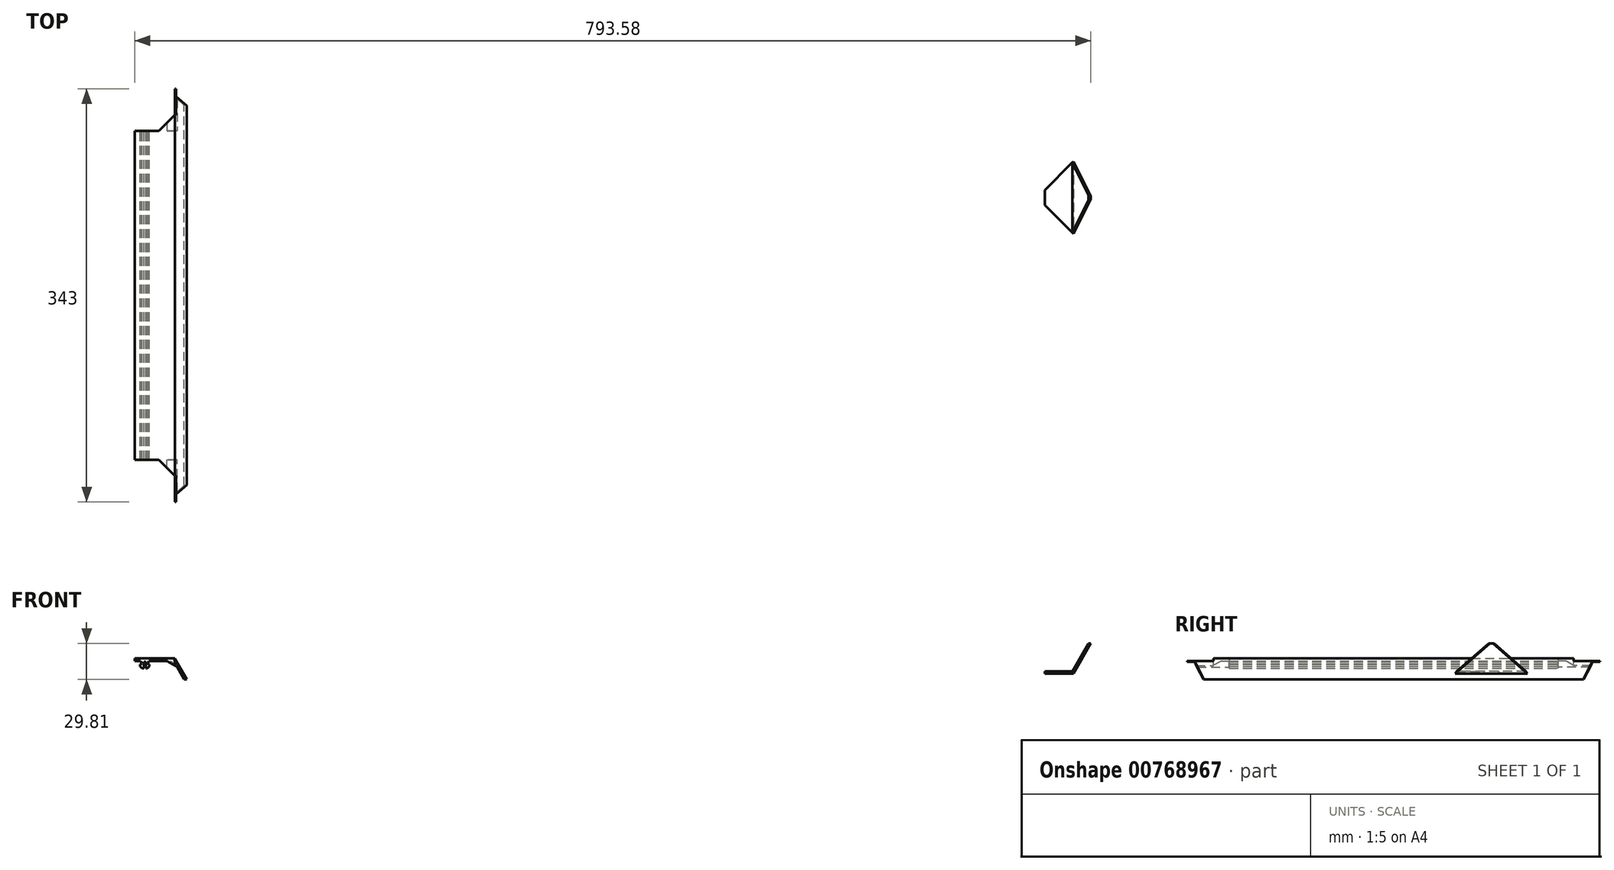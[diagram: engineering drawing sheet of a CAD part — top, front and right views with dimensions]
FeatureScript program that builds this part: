
annotation { "Feature Type Name" : "Feature", "Feature Type Description" : "" }
export const myFeature = defineFeature(function(context is Context, id is Id, definition is map)
    precondition{}
    {
        {
            var Q0;
            Q0=qCreatedBy(makeId("Front.planeOp"),FACE);
            var sketch = newSketch(context, id + "F0", { "sketchPlane" : qUnion([Q0])});
            skLineSegment(sketch, "E0", {"start": v(-133.25, 6.08) * mm, "end": v(-131.79, 4.46) * mm});
            skLineSegment(sketch, "E1", {"start": v(-131.79, 4.46) * mm, "end": v(-130.32, 4.46) * mm});
            skLineSegment(sketch, "E2", {"start": v(-132.9, 10.57) * mm, "end": v(-131.79, 8.3) * mm});
            skLineSegment(sketch, "E3", {"start": v(-133.25, 7.64) * mm, "end": v(-131.79, 8.3) * mm});
            skLineSegment(sketch, "E4", {"start": v(-130.32, 4.46) * mm, "end": v(-130.32, 9.87) * mm});
            skLineSegment(sketch, "E5", {"start": v(-130.32, 9.87) * mm, "end": v(-127.68, 9.87) * mm});
            skLineSegment(sketch, "E6", {"start": v(-134.43, 10.57) * mm, "end": v(-132.9, 10.57) * mm});
            skLineSegment(sketch, "E7.MirrorCS", {"start": v(-124.57, 10.57) * mm, "end": v(-126.1, 10.57) * mm});
            skLineSegment(sketch, "E8.MirrorCS", {"start": v(-126.1, 10.57) * mm, "end": v(-127.2, 8.3) * mm});
            skLineSegment(sketch, "E9.MirrorCS", {"start": v(-125.74, 7.63) * mm, "end": v(-127.2, 8.3) * mm});
            skLineSegment(sketch, "E10.MirrorCS", {"start": v(-125.74, 6.1) * mm, "end": v(-127.2, 4.46) * mm});
            skLineSegment(sketch, "E11.MirrorCS", {"start": v(-127.2, 4.46) * mm, "end": v(-128.68, 4.46) * mm});
            skLineSegment(sketch, "E12.MirrorCS", {"start": v(-128.68, 4.46) * mm, "end": v(-128.68, 9.87) * mm});
            skLineSegment(sketch, "E13.MirrorCS", {"start": v(-128.68, 9.87) * mm, "end": v(-129.5, 9.87) * mm});
            skLineSegment(sketch, "E14", {"start": v(-134.43, 12.57) * mm, "end": v(-124.57, 12.57) * mm});
            skLineSegment(sketch, "E15", {"start": v(-127.68, 9.87) * mm, "end": v(-117.68, 9.87) * mm, "construction": true});
            skLineSegment(sketch, "E16.bottom", {"start": v(-124.57, 12.57) * mm, "end": v(-104.57, 12.57) * mm});
            skLineSegment(sketch, "E16.top", {"start": v(-119.57, 10.57) * mm, "end": v(-111.25, 10.57) * mm});
            skLineSegment(sketch, "E17", {"start": v(-104.57, 12.57) * mm, "end": v(-94.7, -4.81) * mm});
            skLineSegment(sketch, "E18", {"start": v(-94.7, -4.81) * mm, "end": v(-96.7, -4.81) * mm});
            skLineSegment(sketch, "E19", {"start": v(-96.7, -4.81) * mm, "end": v(-102.56, 5.51) * mm});
            skLineSegment(sketch, "E20", {"start": v(-124.57, 10.57) * mm, "end": v(-119.57, 10.57) * mm});
            skLineSegment(sketch, "E21", {"start": v(-127.68, 9.87) * mm, "end": v(-137.68, 9.87) * mm, "construction": true});
            skLineSegment(sketch, "E22.bottom", {"start": v(-134.43, 12.57) * mm, "end": v(-137.68, 12.57) * mm});
            skLineSegment(sketch, "E22.top", {"start": v(-134.43, 10.57) * mm, "end": v(-137.68, 10.57) * mm});
            skLineSegment(sketch, "E22.right", {"start": v(-137.68, 12.57) * mm, "end": v(-137.68, 10.57) * mm});
            skLineSegment(sketch, "E23", {"start": v(-133.25, 7.64) * mm, "end": v(-133.25, 6.08) * mm});
            skLineSegment(sketch, "E24", {"start": v(-125.74, 7.63) * mm, "end": v(-125.74, 6.1) * mm});
            skPoint(sketch, "E25.visualSharp", {"position": v(-105.43, 10.57) * mm});
            skArc(sketch, "E25.filletArc", {"start": v(-102.56, 5.51) * mm, "mid": v(-106.22, 9.22) * mm, "end": v(-111.25, 10.57) * mm});
            skSolve(sketch);
        }
        {
            var Q0;
            Q0 = qSketchRegion(id + "F0", true);
            extrude(context, id + "F1", {"entities" : qUnion([Q0]), "depth" : 273 * mm, "offsetDistance" : 25 * mm});
        }
        {
            var Q0;
            Q0=qCreatedBy(makeId("Top.planeOp"),FACE);
            var sketch = newSketch(context, id + "F2", { "sketchPlane" : qUnion([Q0])});
            skLineSegment(sketch, "E26.bottom", {"start": v(617.8, -25.34) * mm, "end": v(677.8, -25.34) * mm});
            skLineSegment(sketch, "E26.top", {"start": v(617.8, -85.34) * mm, "end": v(677.8, -85.34) * mm});
            skLineSegment(sketch, "E26.left", {"start": v(617.8, -25.34) * mm, "end": v(617.8, -85.34) * mm});
            skLineSegment(sketch, "E26.right", {"start": v(677.8, -25.34) * mm, "end": v(677.8, -85.34) * mm});
            skSolve(sketch);
        }
        {
            var Q0;
            Q0 = qSketchRegion(id + "F2", true);
            extrude(context, id + "F3", {"entities" : qUnion([Q0]), "depth" : 25 * mm, "offsetDistance" : 25 * mm});
        }
        {
            var Q0;
            Q0=makeQuery(id+"F3.opExtrude","SWEPT_FACE",FACE,{"disambiguationData":[OSD([sQuery(id+"F2.wireOp",EDGE,"E26.top")])]});
            var sketch = newSketch(context, id + "F4", { "sketchPlane" : qUnion([Q0])});
            skLineSegment(sketch, "E27", {"start": v(641.7, 0) * mm, "end": v(655.9, 25) * mm});
            skLineSegment(sketch, "E28", {"start": v(653.9, 25) * mm, "end": v(640.84, 2) * mm});
            skLineSegment(sketch, "E29", {"start": v(617.8, 2) * mm, "end": v(640.84, 2) * mm});
            skPoint(sketch, "E30.orphan", {"position": v(639.7, 0) * mm});
            skLineSegment(sketch, "E31", {"start": v(617.8, 2) * mm, "end": v(617.8, 25) * mm});
            skLineSegment(sketch, "E32", {"start": v(617.8, 25) * mm, "end": v(653.9, 25) * mm});
            skLineSegment(sketch, "E33", {"start": v(655.9, 25) * mm, "end": v(677.8, 25) * mm});
            skLineSegment(sketch, "E34", {"start": v(677.8, 25) * mm, "end": v(677.8, 0) * mm});
            skLineSegment(sketch, "E35", {"start": v(677.8, 0) * mm, "end": v(641.7, 0) * mm});
            skSolve(sketch);
        }
        {
            var Q0;
            Q0 = qSketchRegion(id + "F4", true);
            extrude(context, id + "F5", {"entities" : qUnion([Q0]), "operationType" : NewBodyOperationType.REMOVE, "oppositeDirection" : true, "depth" : 60 * mm, "offsetDistance" : 25 * mm});
        }
        {
            var Q0;
            Q0=makeQuery(id+"F3.opExtrude","CAP_FACE",FACE,{"disambiguationData":[OSD([sQuery(id+"F2.wireOp",EDGE,"E26.bottom"),sQuery(id+"F2.wireOp",EDGE,"E26.top"),sQuery(id+"F2.wireOp",EDGE,"E26.left"),sQuery(id+"F2.wireOp",EDGE,"E26.right")])],"isStart":true});
            var sketch = newSketch(context, id + "F6", { "sketchPlane" : qUnion([Q0])});
            skLineSegment(sketch, "E36", {"start": v(641.7, 85.34) * mm, "end": v(617.8, 61.44) * mm});
            skLineSegment(sketch, "E37", {"start": v(641.7, 85.34) * mm, "end": v(617.8, 85.34) * mm});
            skLineSegment(sketch, "E38", {"start": v(641.7, 25.34) * mm, "end": v(617.8, 49.24) * mm});
            skLineSegment(sketch, "E39", {"start": v(641.7, 25.34) * mm, "end": v(617.8, 25.34) * mm});
            skLineSegment(sketch, "E40", {"start": v(617.8, 25.34) * mm, "end": v(617.8, 49.24) * mm});
            skLineSegment(sketch, "E41", {"start": v(617.8, 85.34) * mm, "end": v(617.8, 61.44) * mm});
            skSolve(sketch);
        }
        {
            var Q0;
            Q0 = qSketchRegion(id + "F6", true);
            extrude(context, id + "F7", {"entities" : qUnion([Q0]), "operationType" : NewBodyOperationType.REMOVE, "oppositeDirection" : true, "depth" : 25 * mm, "offsetDistance" : 25 * mm});
        }
        {
            var Q0;
            Q0=makeQuery(id+"F5.boolean.opBoolean","COPY",FACE,{"derivedFrom":makeQuery(id+"F5.opExtrude","SWEPT_FACE",FACE,{"disambiguationData":[OSD([sQuery(id+"F4.wireOp",EDGE,"E27")])]})});
            var sketch = newSketch(context, id + "F8", { "sketchPlane" : qUnion([Q0])});
            skLineSegment(sketch, "E42", {"start": v(-25.34, 317.01) * mm, "end": v(-25.34, 345.76) * mm});
            skLineSegment(sketch, "E43", {"start": v(-25.34, 317.01) * mm, "end": v(-54.09, 345.76) * mm});
            skLineSegment(sketch, "E44", {"start": v(-85.34, 345.76) * mm, "end": v(-85.34, 317.01) * mm});
            skLineSegment(sketch, "E45", {"start": v(-85.34, 317.01) * mm, "end": v(-56.58, 345.76) * mm});
            skLineSegment(sketch, "E46", {"start": v(-25.34, 345.76) * mm, "end": v(-54.09, 345.76) * mm});
            skLineSegment(sketch, "E47", {"start": v(-56.58, 345.76) * mm, "end": v(-85.34, 345.76) * mm});
            skSolve(sketch);
        }
        {
            var Q0;
            Q0 = qSketchRegion(id + "F8", true);
            extrude(context, id + "F9", {"entities" : qUnion([Q0]), "operationType" : NewBodyOperationType.REMOVE, "oppositeDirection" : true, "depth" : 25 * mm, "offsetDistance" : 25 * mm});
        }
        {
            var Q0;
            Q0=makeQuery(id+"F1.opExtrude","CAP_FACE",FACE,{"disambiguationData":[OSD([sQuery(id+"F0.wireOp",EDGE,"E0"),sQuery(id+"F0.wireOp",EDGE,"E1"),sQuery(id+"F0.wireOp",EDGE,"E2"),sQuery(id+"F0.wireOp",EDGE,"E3"),sQuery(id+"F0.wireOp",EDGE,"E4"),sQuery(id+"F0.wireOp",EDGE,"E5"),sQuery(id+"F0.wireOp",EDGE,"E6"),sQuery(id+"F0.wireOp",EDGE,"E7.MirrorCS"),sQuery(id+"F0.wireOp",EDGE,"E8.MirrorCS"),sQuery(id+"F0.wireOp",EDGE,"E9.MirrorCS"),sQuery(id+"F0.wireOp",EDGE,"E10.MirrorCS"),sQuery(id+"F0.wireOp",EDGE,"E11.MirrorCS"),sQuery(id+"F0.wireOp",EDGE,"E12.MirrorCS"),sQuery(id+"F0.wireOp",EDGE,"E13.MirrorCS"),sQuery(id+"F0.wireOp",EDGE,"E14"),sQuery(id+"F0.wireOp",EDGE,"E16.bottom"),sQuery(id+"F0.wireOp",EDGE,"E16.top"),sQuery(id+"F0.wireOp",EDGE,"E17"),sQuery(id+"F0.wireOp",EDGE,"E18"),sQuery(id+"F0.wireOp",EDGE,"E19"),sQuery(id+"F0.wireOp",EDGE,"E20"),sQuery(id+"F0.wireOp",EDGE,"E22.bottom"),sQuery(id+"F0.wireOp",EDGE,"E22.top"),sQuery(id+"F0.wireOp",EDGE,"E22.right"),sQuery(id+"F0.wireOp",EDGE,"E23"),sQuery(id+"F0.wireOp",EDGE,"E24"),sQuery(id+"F0.wireOp",EDGE,"E25.filletArc")])],"isStart":true});
            var sketch = newSketch(context, id + "F10", { "sketchPlane" : qUnion([Q0])});
            skLineSegment(sketch, "E48", {"start": v(96.7, -4.81) * mm, "end": v(94.7, -4.81) * mm});
            skLineSegment(sketch, "E49", {"start": v(94.7, -4.81) * mm, "end": v(104.57, 12.57) * mm});
            skLineSegment(sketch, "E50", {"start": v(104.57, 12.57) * mm, "end": v(117.68, 12.57) * mm});
            skLineSegment(sketch, "E51", {"start": v(117.68, 10.57) * mm, "end": v(111.25, 10.57) * mm});
            skLineSegment(sketch, "E52", {"start": v(111.25, 10.57) * mm, "end": v(102.56, 5.51) * mm});
            skLineSegment(sketch, "E53", {"start": v(102.56, 5.51) * mm, "end": v(96.7, -4.81) * mm});
            skLineSegment(sketch, "E54", {"start": v(137.68, 11.57) * mm, "end": v(117.68, 11.57) * mm, "construction": true});
            skLineSegment(sketch, "E55", {"start": v(117.68, 12.57) * mm, "end": v(117.68, 10.57) * mm});
            skPoint(sketch, "E56.end.orphan", {"position": v(119.44, 10.57) * mm});
            skSolve(sketch);
        }
        {
            var Q0;
            Q0 = qSketchRegion(id + "F10", true);
            extrude(context, id + "F11", {"entities" : qUnion([Q0]), "operationType" : NewBodyOperationType.ADD, "depth" : 35 * mm, "offsetDistance" : 25 * mm});
        }
        {
            var Q0;
            Q0=makeQuery(id+"F1.opExtrude","CAP_FACE",FACE,{"disambiguationData":[OSD([sQuery(id+"F0.wireOp",EDGE,"E0"),sQuery(id+"F0.wireOp",EDGE,"E1"),sQuery(id+"F0.wireOp",EDGE,"E2"),sQuery(id+"F0.wireOp",EDGE,"E3"),sQuery(id+"F0.wireOp",EDGE,"E4"),sQuery(id+"F0.wireOp",EDGE,"E5"),sQuery(id+"F0.wireOp",EDGE,"E6"),sQuery(id+"F0.wireOp",EDGE,"E7.MirrorCS"),sQuery(id+"F0.wireOp",EDGE,"E8.MirrorCS"),sQuery(id+"F0.wireOp",EDGE,"E9.MirrorCS"),sQuery(id+"F0.wireOp",EDGE,"E10.MirrorCS"),sQuery(id+"F0.wireOp",EDGE,"E11.MirrorCS"),sQuery(id+"F0.wireOp",EDGE,"E12.MirrorCS"),sQuery(id+"F0.wireOp",EDGE,"E13.MirrorCS"),sQuery(id+"F0.wireOp",EDGE,"E14"),sQuery(id+"F0.wireOp",EDGE,"E16.bottom"),sQuery(id+"F0.wireOp",EDGE,"E16.top"),sQuery(id+"F0.wireOp",EDGE,"E17"),sQuery(id+"F0.wireOp",EDGE,"E18"),sQuery(id+"F0.wireOp",EDGE,"E19"),sQuery(id+"F0.wireOp",EDGE,"E20"),sQuery(id+"F0.wireOp",EDGE,"E22.bottom"),sQuery(id+"F0.wireOp",EDGE,"E22.top"),sQuery(id+"F0.wireOp",EDGE,"E22.right"),sQuery(id+"F0.wireOp",EDGE,"E23"),sQuery(id+"F0.wireOp",EDGE,"E24"),sQuery(id+"F0.wireOp",EDGE,"E25.filletArc")])],"isStart":false});
            var sketch = newSketch(context, id + "F12", { "sketchPlane" : qUnion([Q0])});
            skLineSegment(sketch, "E57", {"start": v(-137.68, 11.57) * mm, "end": v(-117.68, 11.57) * mm, "construction": true});
            skLineSegment(sketch, "E58", {"start": v(-117.68, 12.57) * mm, "end": v(-117.68, 10.57) * mm});
            skLineSegment(sketch, "E59", {"start": v(-117.68, 10.57) * mm, "end": v(-111.25, 10.57) * mm});
            skLineSegment(sketch, "E60", {"start": v(-111.25, 10.57) * mm, "end": v(-102.56, 5.51) * mm});
            skLineSegment(sketch, "E61", {"start": v(-102.56, 5.51) * mm, "end": v(-96.7, -4.81) * mm});
            skLineSegment(sketch, "E62", {"start": v(-96.7, -4.81) * mm, "end": v(-94.7, -4.81) * mm});
            skLineSegment(sketch, "E63", {"start": v(-94.7, -4.81) * mm, "end": v(-104.57, 12.57) * mm});
            skLineSegment(sketch, "E64", {"start": v(-104.57, 12.57) * mm, "end": v(-117.68, 12.57) * mm});
            skSolve(sketch);
        }
        {
            var Q0;
            Q0 = qSketchRegion(id + "F12", true);
            extrude(context, id + "F13", {"entities" : qUnion([Q0]), "operationType" : NewBodyOperationType.ADD, "depth" : 35 * mm, "offsetDistance" : 25 * mm});
        }
        {
            var Q0;
            Q0=makeQuery(id+"F13.boolean.opBoolean","MERGE",FACE,{"derivedFrom":[makeQuery(id+"F11.boolean.opBoolean","MERGE",FACE,{"derivedFrom":[makeQuery(id+"F1.opExtrude","SWEPT_FACE",FACE,{"disambiguationData":[OSD([sQuery(id+"F0.wireOp",EDGE,"E14"),sQuery(id+"F0.wireOp",EDGE,"E16.bottom"),sQuery(id+"F0.wireOp",EDGE,"E22.bottom")])]}),makeQuery(id+"F11.opExtrude","SWEPT_FACE",FACE,{"disambiguationData":[OSD([sQuery(id+"F10.wireOp",EDGE,"E50")])]})]}),makeQuery(id+"F13.opExtrude","SWEPT_FACE",FACE,{"disambiguationData":[OSD([sQuery(id+"F12.wireOp",EDGE,"E64")])]})]});
            var sketch = newSketch(context, id + "F14", { "sketchPlane" : qUnion([Q0])});
            skLineSegment(sketch, "E65", {"start": v(-117.68, 0) * mm, "end": v(-109.5, 0) * mm});
            skLineSegment(sketch, "E66", {"start": v(-117.68, 0) * mm, "end": v(-104.57, 13.1) * mm});
            skLineSegment(sketch, "E67", {"start": v(-104.57, 13.1) * mm, "end": v(-104.57, 35) * mm});
            skLineSegment(sketch, "E68", {"start": v(-104.57, 35) * mm, "end": v(-117.68, 35) * mm});
            skLineSegment(sketch, "E69", {"start": v(-117.68, 35) * mm, "end": v(-117.68, 0) * mm});
            skLineSegment(sketch, "E70", {"start": v(-117.68, -273) * mm, "end": v(-110.08, -273) * mm});
            skLineSegment(sketch, "E71", {"start": v(-117.68, -273) * mm, "end": v(-104.57, -286.1) * mm});
            skLineSegment(sketch, "E72", {"start": v(-104.57, -286.1) * mm, "end": v(-104.57, -308) * mm});
            skLineSegment(sketch, "E73", {"start": v(-104.57, -308) * mm, "end": v(-117.68, -308) * mm});
            skLineSegment(sketch, "E74", {"start": v(-117.68, -308) * mm, "end": v(-117.68, -273) * mm});
            skSolve(sketch);
        }
        {
            var Q0;
            Q0 = qSketchRegion(id + "F14", true);
            extrude(context, id + "F15", {"entities" : qUnion([Q0]), "operationType" : NewBodyOperationType.REMOVE, "oppositeDirection" : true, "depth" : 25 * mm, "offsetDistance" : 25 * mm});
        }
        {
            var Q0;
            Q0=makeQuery(id+"F13.opExtrude","CAP_FACE",FACE,{"disambiguationData":[OSD([sQuery(id+"F12.wireOp",EDGE,"E58"),sQuery(id+"F12.wireOp",EDGE,"E59"),sQuery(id+"F12.wireOp",EDGE,"E60"),sQuery(id+"F12.wireOp",EDGE,"E61"),sQuery(id+"F12.wireOp",EDGE,"E62"),sQuery(id+"F12.wireOp",EDGE,"E63"),sQuery(id+"F12.wireOp",EDGE,"E64")])],"isStart":false});
            var sketch = newSketch(context, id + "F16", { "sketchPlane" : qUnion([Q0])});
            skLineSegment(sketch, "E75.bottom", {"start": v(-83.95, 21.16) * mm, "end": v(-118.74, 21.16) * mm});
            skLineSegment(sketch, "E75.top", {"start": v(-83.95, 10.51) * mm, "end": v(-118.74, 10.51) * mm});
            skLineSegment(sketch, "E75.left", {"start": v(-83.95, 21.16) * mm, "end": v(-83.95, 10.51) * mm});
            skLineSegment(sketch, "E75.right", {"start": v(-118.74, 21.16) * mm, "end": v(-118.74, 10.51) * mm});
            skSolve(sketch);
        }
        {
            var Q0;
            Q0 = qSketchRegion(id + "F16", true);
            extrude(context, id + "F17", {"entities" : qUnion([Q0]), "operationType" : NewBodyOperationType.REMOVE, "oppositeDirection" : true, "depth" : 22 * mm, "offsetDistance" : 25 * mm});
        }
        {
            var Q0;
            Q0=makeQuery(id+"F11.opExtrude","CAP_FACE",FACE,{"disambiguationData":[OSD([sQuery(id+"F10.wireOp",EDGE,"E48"),sQuery(id+"F10.wireOp",EDGE,"E49"),sQuery(id+"F10.wireOp",EDGE,"E50"),sQuery(id+"F10.wireOp",EDGE,"E51"),sQuery(id+"F10.wireOp",EDGE,"E52"),sQuery(id+"F10.wireOp",EDGE,"E53"),sQuery(id+"F10.wireOp",EDGE,"E55")])],"isStart":false});
            var sketch = newSketch(context, id + "F18", { "sketchPlane" : qUnion([Q0])});
            skLineSegment(sketch, "E76.bottom", {"start": v(90.84, 18.7) * mm, "end": v(118.96, 18.7) * mm});
            skLineSegment(sketch, "E76.top", {"start": v(90.84, 10.51) * mm, "end": v(118.96, 10.51) * mm});
            skLineSegment(sketch, "E76.left", {"start": v(90.84, 18.7) * mm, "end": v(90.84, 10.51) * mm});
            skLineSegment(sketch, "E76.right", {"start": v(118.96, 18.7) * mm, "end": v(118.96, 10.51) * mm});
            skSolve(sketch);
        }
        {
            var Q0;
            Q0 = qSketchRegion(id + "F18", true);
            extrude(context, id + "F19", {"entities" : qUnion([Q0]), "operationType" : NewBodyOperationType.REMOVE, "oppositeDirection" : true, "depth" : 22 * mm, "offsetDistance" : 25 * mm});
        }
        {
            var Q0;
            Q0=makeQuery(id+"F13.boolean.opBoolean","MERGE",FACE,{"derivedFrom":[makeQuery(id+"F11.boolean.opBoolean","MERGE",FACE,{"derivedFrom":[makeQuery(id+"F1.opExtrude","SWEPT_FACE",FACE,{"disambiguationData":[OSD([sQuery(id+"F0.wireOp",EDGE,"E17")])]}),makeQuery(id+"F11.opExtrude","SWEPT_FACE",FACE,{"disambiguationData":[OSD([sQuery(id+"F10.wireOp",EDGE,"E49")])]})]}),makeQuery(id+"F13.opExtrude","SWEPT_FACE",FACE,{"disambiguationData":[OSD([sQuery(id+"F12.wireOp",EDGE,"E63")])]})]});
            var sketch = newSketch(context, id + "F20", { "sketchPlane" : qUnion([Q0])});
            skLineSegment(sketch, "E77", {"start": v(-301.63, 60.22) * mm, "end": v(-293.95, 42.6) * mm});
            skLineSegment(sketch, "E78", {"start": v(-136.5, 62.6) * mm, "end": v(-136.5, 42.6) * mm, "construction": true});
            skLineSegment(sketch, "E79", {"start": v(-293.95, 42.6) * mm, "end": v(-308, 42.6) * mm});
            skLineSegment(sketch, "E80", {"start": v(-308, 42.6) * mm, "end": v(-308, 60.22) * mm});
            skLineSegment(sketch, "E81", {"start": v(-308, 60.22) * mm, "end": v(-301.63, 60.22) * mm});
            skLineSegment(sketch, "E82.MirrorCS", {"start": v(28.63, 60.22) * mm, "end": v(20.95, 42.6) * mm});
            skLineSegment(sketch, "E83.MirrorCS", {"start": v(35, 42.6) * mm, "end": v(35, 60.22) * mm});
            skLineSegment(sketch, "E84.MirrorCS", {"start": v(20.95, 42.6) * mm, "end": v(35, 42.6) * mm});
            skLineSegment(sketch, "E85.MirrorCS", {"start": v(35, 60.22) * mm, "end": v(28.63, 60.22) * mm});
            skSolve(sketch);
        }
        {
            var Q0;
            Q0 = qSketchRegion(id + "F20", true);
            extrude(context, id + "F21", {"entities" : qUnion([Q0]), "operationType" : NewBodyOperationType.REMOVE, "oppositeDirection" : true, "depth" : 25 * mm, "offsetDistance" : 25 * mm});
        }
    });
